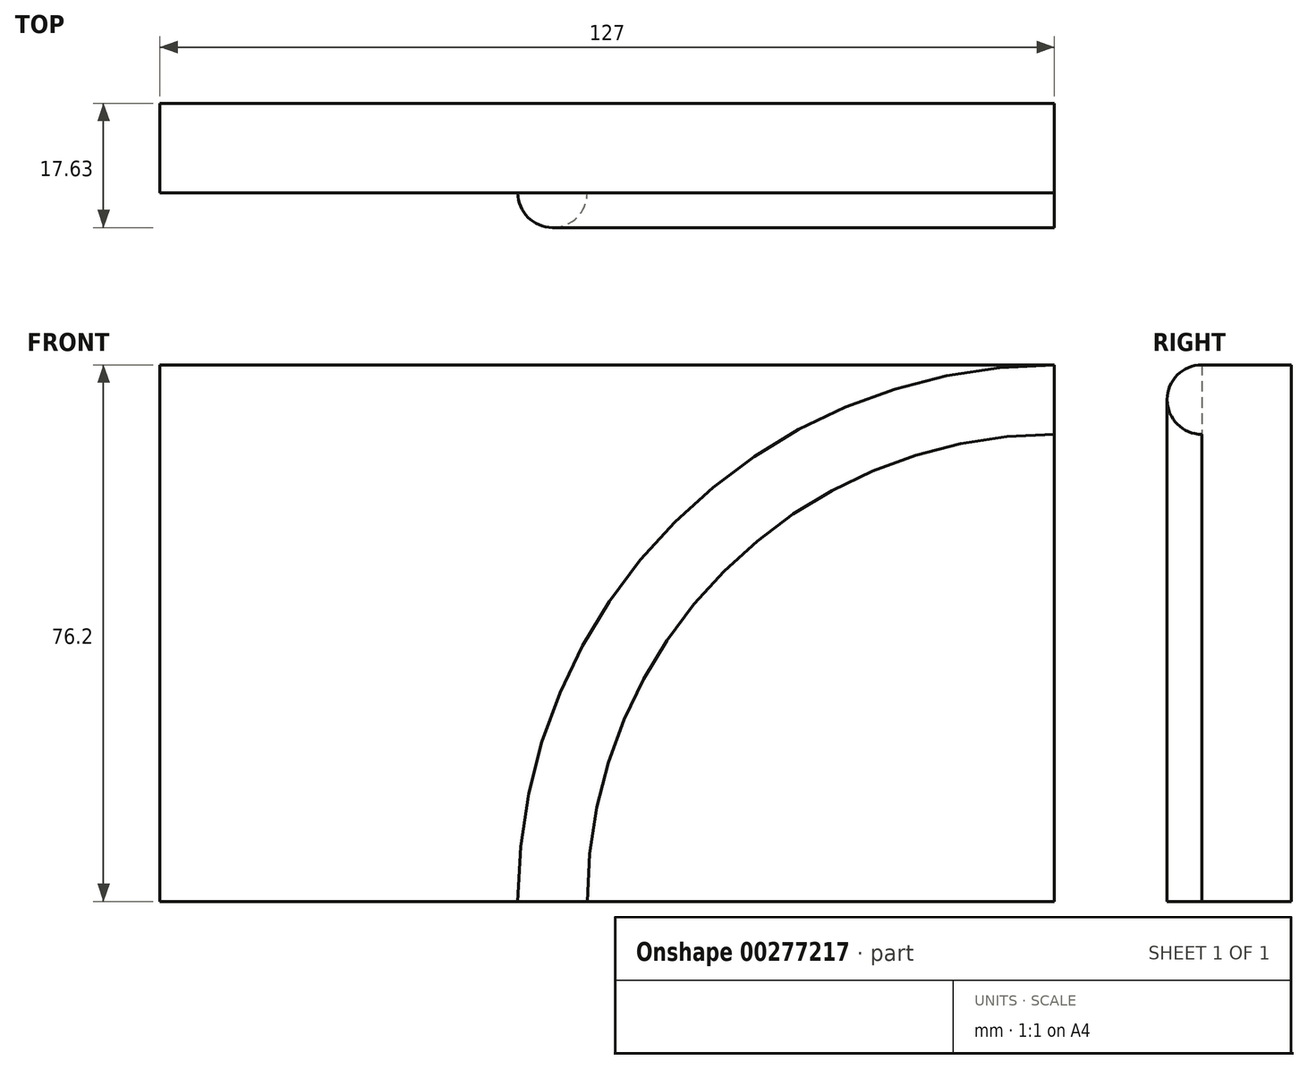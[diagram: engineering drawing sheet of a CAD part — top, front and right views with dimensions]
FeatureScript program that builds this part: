
annotation { "Feature Type Name" : "Feature", "Feature Type Description" : "" }
export const myFeature = defineFeature(function(context is Context, id is Id, definition is map)
    precondition{}
    {
        {
            var Q0;
            Q0=qCreatedBy(makeId("Front.planeOp"),FACE);
            var sketch = newSketch(context, id + "F0", { "sketchPlane" : qUnion([Q0])});
            skLineSegment(sketch, "E0.bottom", {"start": v(63.5, 38.1) * mm, "end": v(-63.5, 38.1) * mm});
            skLineSegment(sketch, "E0.top", {"start": v(63.5, -38.1) * mm, "end": v(-63.5, -38.1) * mm});
            skLineSegment(sketch, "E0.left", {"start": v(63.5, 38.1) * mm, "end": v(63.5, -38.1) * mm});
            skLineSegment(sketch, "E0.right", {"start": v(-63.5, 38.1) * mm, "end": v(-63.5, -38.1) * mm});
            skPoint(sketch, "E0.middle", {"position": v(0, 0) * mm});
            skSolve(sketch);
        }
        {
            var Q0;
            Q0=makeQuery(id+"F0.imprint","IMPRINT",FACE,{"disambiguationData":[TD([[makeQuery(id+"F0.imprint","IMPRINT",EDGE,{"derivedFrom":sQuery(id+"F0.wireOp",EDGE,"E0.bottom")}),1.0]])]});
            extrude(context, id + "F1", {"entities" : qUnion([Q0]), "depth" : 12.7 * mm});
        }
        {
            var Q0;
            Q0=makeQuery(id+"F1.opExtrude","CAP_FACE",FACE,{"disambiguationData":[OSD([sQuery(id+"F0.wireOp",EDGE,"E0.bottom"),sQuery(id+"F0.wireOp",EDGE,"E0.top"),sQuery(id+"F0.wireOp",EDGE,"E0.left"),sQuery(id+"F0.wireOp",EDGE,"E0.right")])],"isStart":false});
            var sketch = newSketch(context, id + "F2", { "sketchPlane" : qUnion([Q0])});
            skArc(sketch, "E1", {"start": v(63.5, 38.1) * mm, "mid": v(9.62, 15.78) * mm, "end": v(-12.7, -38.1) * mm});
            skArc(sketch, "E2", {"start": v(63.5, 27.94) * mm, "mid": v(16.8, 8.6) * mm, "end": v(-2.54, -38.1) * mm});
            skArc(sketch, "E3", {"start": v(63.5, 33.02) * mm, "mid": v(13.21, 12.19) * mm, "end": v(-7.62, -38.1) * mm});
            skSolve(sketch);
        }
        {
            var Q0;
            Q0=makeQuery(id+"F1.opExtrude","SWEPT_FACE",FACE,{"disambiguationData":[OSD([sQuery(id+"F0.wireOp",EDGE,"E0.left")])]});
            var sketch = newSketch(context, id + "F3", { "sketchPlane" : qUnion([Q0])});
            skArc(sketch, "E4", {"start": v(-12.7, 38.1) * mm, "mid": v(-17.63, 33.17) * mm, "end": v(-12.7, 28.23) * mm});
            skSolve(sketch);
        }
        {
            var Q0;
            {var subQ0=sQuery(id+"F3.wireOp",EDGE,"E4");Q0=makeQuery(id+"F3.imprint","IMPRINT",FACE,{"disambiguationData":[TD([[makeQuery(id+"F3.imprint","IMPRINT",EDGE,{"derivedFrom":subQ0}),1.0]])]});}
            var Q1;
            Q1=sQuery(id+"F2.wireOp",EDGE,"E3");
            sweep(context, id + "F4", {"operationType" : NewBodyOperationType.ADD, "profiles" : qUnion([Q0]), "path" : qUnion([Q1])});
        }
    });
